FCSTD DOCUMENT  (FreeCAD 0.15R4344 (Git))
Label: v-slot
License: CC-BY 3.0
LicenseURL: http://creativecommons.org/licenses/by/3.0/
objects: Sketcher::SketchObject×1
note: 1 computed .brp shape members not serialized (recipe doc carries the construction recipe); baked Part::Feature solids carry a one-line shape summary decoded from their .brp

FEATURE [Sketcher::SketchObject] Sketch
  sketch-geometry (29):
    g0: LineSegment StartX=-8.5 StartY=10 StartZ=0 EndX=8.5 EndY=10 EndZ=0
    g1: LineSegment StartX=10 StartY=8.5 StartZ=0 EndX=10 EndY=-8.5 EndZ=0
    g2: LineSegment StartX=8.5 StartY=-10 StartZ=0 EndX=-8.5 EndY=-10 EndZ=0
    g3: LineSegment StartX=-10 StartY=-8.5 StartZ=0 EndX=-10 EndY=8.5 EndZ=0
    g4: ArcOfCircle CenterX=8.5 CenterY=8.5 CenterZ=0 NormalX=0 NormalY=0 NormalZ=1 Radius=1.5 StartAngle=0 EndAngle=1.5708
    g5: ArcOfCircle CenterX=8.5 CenterY=-8.5 CenterZ=0 NormalX=0 NormalY=0 NormalZ=1 Radius=1.5 StartAngle=4.71239 EndAngle=6.28319
    g6: ArcOfCircle CenterX=-8.5 CenterY=-8.5 CenterZ=0 NormalX=0 NormalY=0 NormalZ=1 Radius=1.5 StartAngle=3.14159 EndAngle=4.71239
    g7: ArcOfCircle CenterX=-8.5 CenterY=8.5 CenterZ=0 NormalX=0 NormalY=0 NormalZ=1 Radius=1.5 StartAngle=1.5708 EndAngle=3.14159
    g8: Circle CenterX=0 CenterY=0 CenterZ=0 NormalX=0 NormalY=0 NormalZ=1 Radius=1.05
    g9: LineSegment StartX=-4 StartY=4 StartZ=0 EndX=4 EndY=4 EndZ=0
    g10: LineSegment StartX=4 StartY=4 StartZ=0 EndX=4 EndY=-4 EndZ=0
    g11: LineSegment StartX=4 StartY=-4 StartZ=0 EndX=-4 EndY=-4 EndZ=0
    g12: LineSegment StartX=-4 StartY=-4 StartZ=0 EndX=-4 EndY=4 EndZ=0
    g13: LineSegment StartX=-8.4 StartY=-8.4 StartZ=0 EndX=8.4 EndY=-8.4 EndZ=0
    g14: LineSegment StartX=8.4 StartY=-8.4 StartZ=0 EndX=8.4 EndY=8.4 EndZ=0
    g15: LineSegment StartX=8.4 StartY=8.4 StartZ=0 EndX=-8.4 EndY=8.4 EndZ=0
    g16: LineSegment StartX=-8.4 StartY=8.4 StartZ=0 EndX=-8.4 EndY=-8.4 EndZ=0
    g17: LineSegment StartX=4 StartY=4 StartZ=0 EndX=8.5 EndY=8.5 EndZ=0
    g18: LineSegment StartX=2.23804 StartY=8.4 StartZ=0 EndX=3.83804 EndY=10 EndZ=0
    g19: LineSegment StartX=-8.4 StartY=8.4 StartZ=0 EndX=-4 EndY=4 EndZ=0
    g20: LineSegment StartX=-4 StartY=-4 StartZ=0 EndX=-8.39891 EndY=-8.39891 EndZ=0
    g21: LineSegment StartX=4 StartY=-4 StartZ=0 EndX=8.5 EndY=-8.5 EndZ=0
    g22: LineSegment StartX=-4.31477 StartY=10 StartZ=0 EndX=-2.71477 EndY=8.4 EndZ=0
    g23: LineSegment StartX=-12.5322 StartY=6.26474 StartZ=0 EndX=-6.86964 EndY=0.602132 EndZ=0
    g24: LineSegment StartX=-6.9099 StartY=-2.07064 StartZ=0 EndX=-12.261 EndY=-6.53765 EndZ=0
    g25: LineSegment StartX=-6.86337 StartY=-12.1214 StartZ=0 EndX=-2.34983 EndY=-7.37522 EndZ=0
    g26: LineSegment StartX=5.74662 StartY=-11.5165 StartZ=0 EndX=1.97758 EndY=-7.32869 EndZ=0
    g27: LineSegment StartX=12.5052 StartY=-6.29402 StartZ=0 EndX=7.15391 EndY=-0.942765 EndZ=0
    g28: LineSegment StartX=6.92223 StartY=0.206221 StartZ=0 EndX=12.3049 EndY=5.58887 EndZ=0
  constraints (71):
    c: Horizontal(g0)
    c: Horizontal(g2)
    c: Vertical(g1)
    c: Vertical(g3)
    c: Tangent(g0,g4)
    c: Tangent(g1,g4)
    c: Tangent(g1,g5)
    c: Tangent(g2,g5)
    c: Tangent(g2,g6)
    c: Tangent(g3,g6)
    c: Tangent(g3,g7)
    c: Tangent(g0,g7)
    c: Radius(g7) = 1.5
    c: Radius(g4) = 1.5
    c: Radius(g5) = 1.5
    c: Radius(g6) = 1.5
    c: Equal(g0,g3)
    c: DistanceY(g-1,g0) = 10
    c: DistanceX(g-1,g3) = -10
    c: DistanceX(g-1,g1) = 10
    c: Coincident(g8,g-1)
    c: Radius(g8) = 1.05
    c: Coincident(g9,g10)
    c: Coincident(g10,g11)
    c: Coincident(g11,g12)
    c: Coincident(g12,g9)
    c: Horizontal(g9)
    c: Horizontal(g11)
    c: Vertical(g10)
    c: Vertical(g12)
    c: Equal(g9,g12)
    c: DistanceX(g-1,g9) = -4
    c: DistanceY(g-1,g9) = 4
    c: Coincident(g13,g14)
    c: Coincident(g14,g15)
    c: Coincident(g15,g16)
    c: Coincident(g16,g13)
    c: Horizontal(g13)
    c: Horizontal(g15)
    c: Vertical(g14)
    c: Vertical(g16)
    c: Equal(g16,g15)
    c: DistanceY(g-1,g15) = 8.4
    c: DistanceX(g-1,g15) = -8.4
    c: DistanceX(g15) = -16.8
    c: Coincident(g17,g9)
    c: Coincident(g17,g4)
    c: Parallel(g17,g18)
    c: Coincident(g19,g15)
    c: Coincident(g19,g9)
    c: Coincident(g20,g11)
    c: Parallel(g19,g22)
    c: PointOnObject(g18,g15)
    c: PointOnObject(g18,g0)
    c: PointOnObject(g22,g0)
    c: PointOnObject(g22,g15)
    c: Parallel(g17,g28)
    c: Coincident(g21,g10)
    c: DistanceX(g9) = 8
    c: Parallel(g21,g27)
    c: Parallel(g19,g23)
    c: Coincident(g21,g5)
    c: Coincident(g6,g13)
    c: Coincident(g6,g16)
    c: Coincident(g6,g20)
    c: Parallel(g20,g24)
    c: Parallel(g20,g25)
    c: Parallel(g21,g26)
    c: PointOnObject(g23,g16)
    c: PointOnObject(g23,g3)
    c: PointOnObject(g28,g1)
